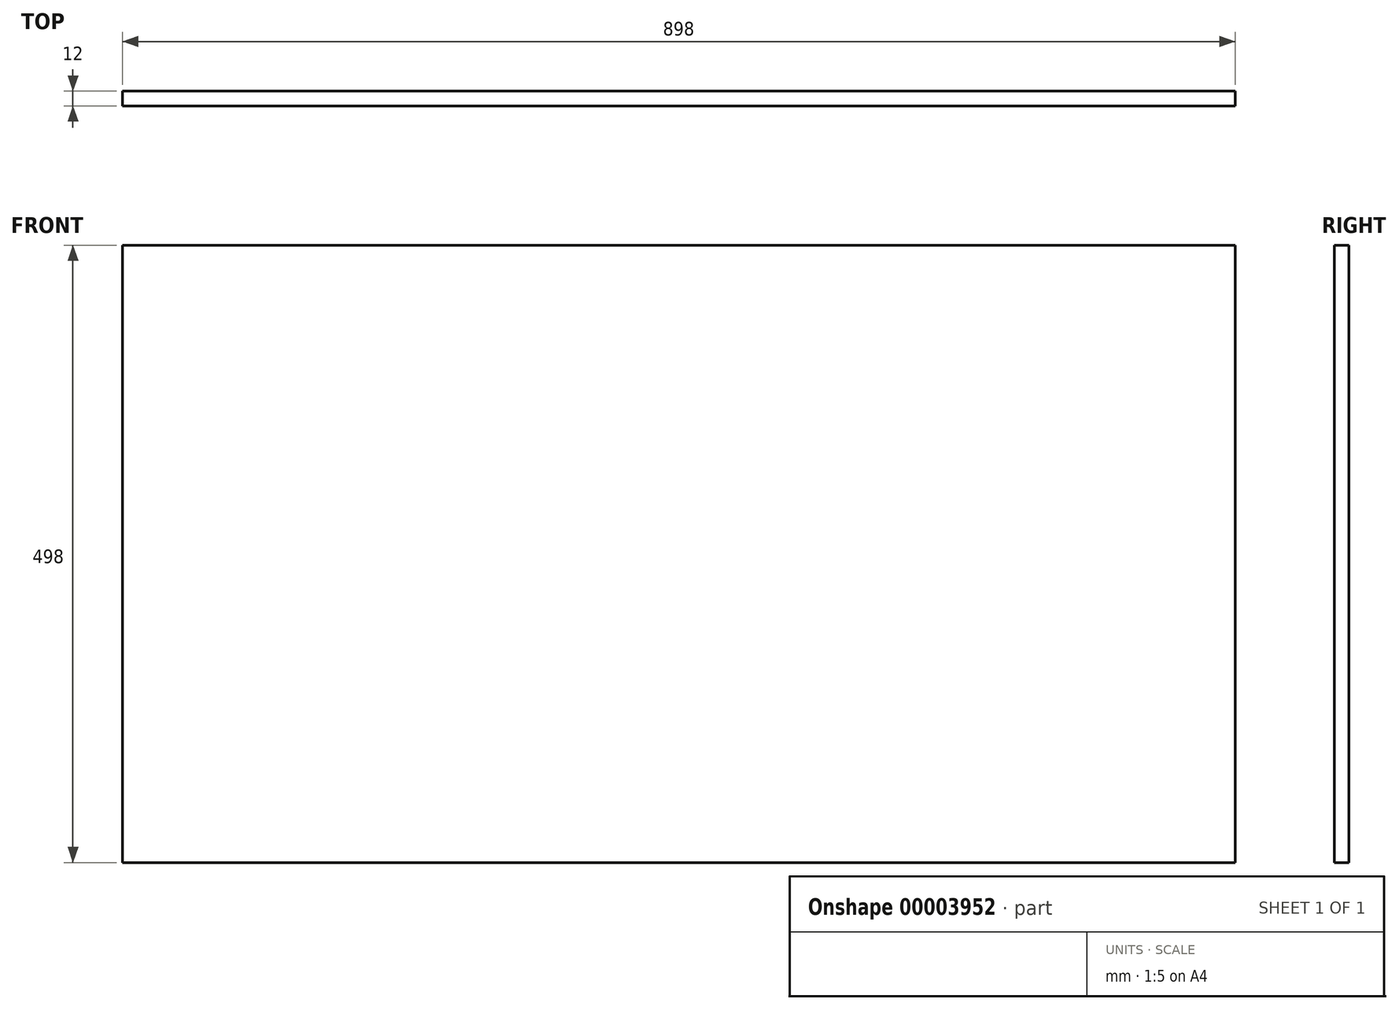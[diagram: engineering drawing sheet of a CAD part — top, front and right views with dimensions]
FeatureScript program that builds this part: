
annotation { "Feature Type Name" : "Feature", "Feature Type Description" : "" }
export const myFeature = defineFeature(function(context is Context, id is Id, definition is map)
    precondition{}
    {
        {
            var Q0;
            Q0=qCreatedBy(makeId("Front.planeOp"),FACE);
            var sketch = newSketch(context, id + "F0", { "sketchPlane" : qUnion([Q0])});
            skLineSegment(sketch, "E0.bottom", {"start": v(0, 0) * mm, "end": v(898, 0) * mm});
            skLineSegment(sketch, "E0.top", {"start": v(0, 498) * mm, "end": v(898, 498) * mm});
            skLineSegment(sketch, "E0.left", {"start": v(0, 0) * mm, "end": v(0, 498) * mm});
            skLineSegment(sketch, "E0.right", {"start": v(898, 0) * mm, "end": v(898, 498) * mm});
            skSolve(sketch);
        }
        {
            var Q0;
            Q0=makeQuery(id+"F0.imprint","IMPRINT",FACE,{"disambiguationData":[TD([[makeQuery(id+"F0.imprint","IMPRINT",EDGE,{"derivedFrom":sQuery(id+"F0.wireOp",EDGE,"E0.bottom")}),1.0]])]});
            extrude(context, id + "F1", {"entities" : qUnion([Q0]), "depth" : 12 * mm});
        }
    });
